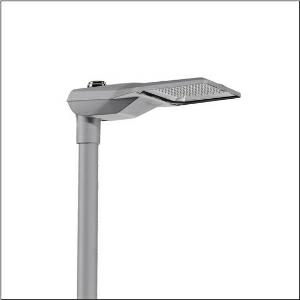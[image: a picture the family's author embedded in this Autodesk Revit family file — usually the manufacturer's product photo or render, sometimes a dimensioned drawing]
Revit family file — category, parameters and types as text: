
# Revit family: streetlight_sl_21_midi___p0_8a_5xe7u57n08nb_0f41
name_source: partatom
category: Lighting Fixtures
units: mm (PartAtom-declared; Revit-internal decimal feet)

## family parameters
Cut with Voids When Loaded = No
Host = Face
Light Source = No
Part Type = Normal
Room Calculation Point = No
Round Connector Dimension = Use Diameter
Shared = No

## types (1)
- --- (1 x LED, 19690 lm, 151.2 W, 3000K)
    Apparent Load = 151 VA
    CIE Flux Codes = 36 69 97 100 100
    Color Rendering = 80
    Color Temperature = 3000K
    Default Elevation = 1800 mm
    Description = Streetlight SL 21 midi, mast luminaire, primary light control with lens, of PMMA, primary optical cover: cover, of toughened safety glass, transparent, light distribution: P0.8a, light emission: direct distribution, primary light characteristic: asymmetric, installation type: side-entry, LED, 3G 2.5mm², High Power LED, rated luminous flux: 19.690lm, luminous efficacy: 130lm/W, light colour: 830, colour temperature: 3000K, control gear: NEMA (7pin), control: flexible luminous flux parameterisation, time-dependent luminous flux control, constant luminous flux control, pre-setting: linear dimming characteristic, overheat protection, mains connection: 220..240V, AC, 50/60Hz, connection cable pre-assembled, cable length: 12,5m, wiring characteristics: H05VV-F, start of lifetime: 151W, end of service life: 157W, reduction: 70W, luminaire housing, of diecast aluminium (EN AC-44300), powder-coated, Siteco® metallic grey (DB 702S), corrosivity category C5 mid according to DIN EN ISO 12944, multi-level sealing system, sealing non-destructively replaceable, inclination adjustable: 0°, 5°, 10°, 15°, length: 644mm, width: 335mm, height: 110mm, spigot size: 42mm (side-entry), mounting height: 4..8m, protection rating (complete): IP66, insulation class (complete): insulation class I (protective earthing), certification: CE, ENEC, ENEC+, VDE, impact resistance: IK10, permissible operating ambient temperature for outdoor applications: -40..+50°C, standard-compliant lighting for roads and squares, packaging unit: 1 piece

Light Distribution: P0.8a
    Height = 111 mm
    Lamp = 1 x LED
    Lamp Light Flux = 19690 lm
    Lamp Power = 151.2 W
    Lamp count = 1
    Length = 644 mm
    Luminous efficacy = 130 lm/W
    Manufacturer = Siteco
    ModVariant = No
    Model = 5XE7U57N08NB
    Number of Poles = 1
    OnlyDefault = Yes
    Power Factor = 1
    Product Name = Streetlight SL 21 midi | P0.8a
    Product group = mast luminaire | pylon top
    ProductGroupID = 6100
    Protection Class = Protection class I
    Protection Degree = IP 66
    RLX_Detail_Level = 1
    RLX_Emergency_Light_Flux = 0 lm
    RLX_Emergency_Type = 0
    RLX_Emergency_Type_DB = No
    RlxData = <blob elided: 26441 chars, md5=df566745>
    Socket = socket
    Standby Power = 0 W
    System Light Flux = 19689 lm
    System Power = 151 W
    Type Comments = factory setting: luminous flux: 100 % | dim-lin: 254 | 802 mA
    Type Image = l_1294377.jpg
    URL = http://relux.com
    VarID = @adj_071710
    Voltage = 0 V
    Weight = 0.00 kg
    Width = 336 mm

## geometry (parser evidence)
native form markers: Blend x4, Sweep x13
no freeform markers — native parametric forms only
